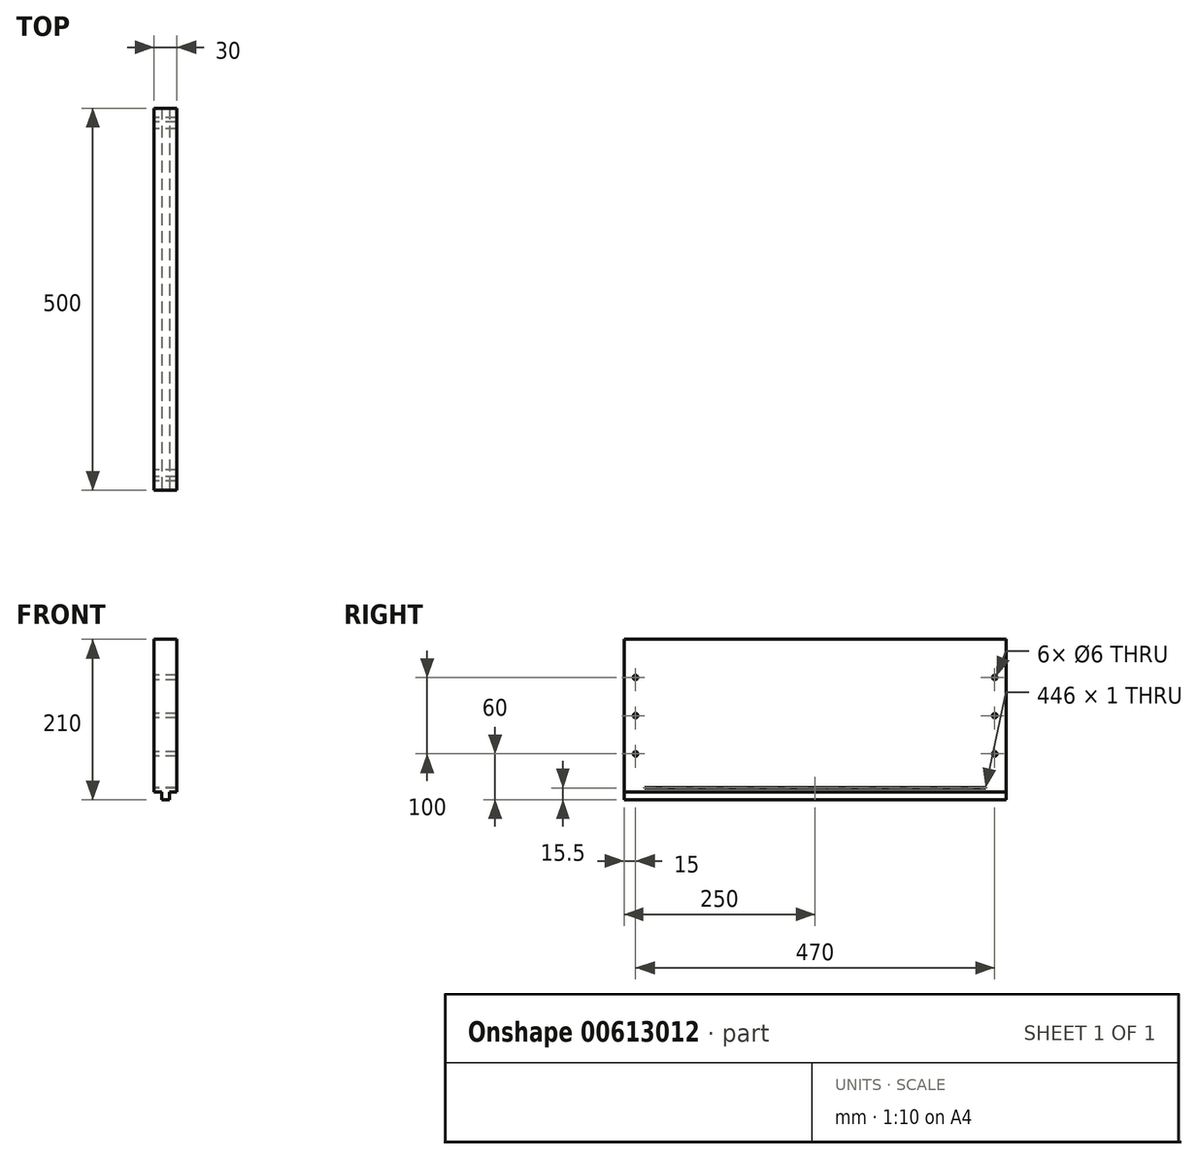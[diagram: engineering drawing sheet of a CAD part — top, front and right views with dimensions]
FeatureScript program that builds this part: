
annotation { "Feature Type Name" : "Feature", "Feature Type Description" : "" }
export const myFeature = defineFeature(function(context is Context, id is Id, definition is map)
    precondition{}
    {
        {
            var Q0;
            Q0=qCreatedBy(makeId("Right.planeOp"),FACE);
            var sketch = newSketch(context, id + "F0", { "sketchPlane" : qUnion([Q0])});
            skLineSegment(sketch, "E0.bottom", {"start": v(250, -100) * mm, "end": v(-250, -100) * mm});
            skLineSegment(sketch, "E0.top", {"start": v(250, 100) * mm, "end": v(-250, 100) * mm});
            skLineSegment(sketch, "E0.left", {"start": v(250, -100) * mm, "end": v(250, 100) * mm});
            skLineSegment(sketch, "E0.right", {"start": v(-250, -100) * mm, "end": v(-250, 100) * mm});
            skPoint(sketch, "E0.middle", {"position": v(0, 0) * mm});
            skCircle(sketch, "E1", {"center": v(-235, 50) * mm, "radius": 3 * mm});
            skCircle(sketch, "E2", {"center": v(235, -50) * mm, "radius": 3 * mm});
            skCircle(sketch, "E3", {"center": v(235, 50) * mm, "radius": 3 * mm});
            skCircle(sketch, "E4", {"center": v(-235, -50) * mm, "radius": 3 * mm});
            skCircle(sketch, "E5", {"center": v(-235, 0) * mm, "radius": 3 * mm});
            skCircle(sketch, "E6", {"center": v(235, 0) * mm, "radius": 3 * mm});
            skSolve(sketch);
        }
        {
            var Q0;
            Q0=qSketchRegion(id+"F0",true);
            extrude(context, id + "F1", {"entities" : qUnion([Q0]), "depth" : 30 * mm, "offsetDistance" : 25 * mm});
        }
        {
            var Q0;
            Q0=makeQuery(id+"F1.opExtrude","SWEPT_FACE",FACE,{"disambiguationData":[OSD([sQuery(id+"F0.wireOp",EDGE,"E0.right")])]});
            var sketch = newSketch(context, id + "F2", { "sketchPlane" : qUnion([Q0])});
            skLineSegment(sketch, "E7.bottom", {"start": v(20, -110) * mm, "end": v(10, -110) * mm});
            skLineSegment(sketch, "E7.top", {"start": v(20, -100) * mm, "end": v(10, -100) * mm});
            skLineSegment(sketch, "E7.left", {"start": v(20, -110) * mm, "end": v(20, -100) * mm});
            skLineSegment(sketch, "E7.right", {"start": v(10, -110) * mm, "end": v(10, -100) * mm});
            skPoint(sketch, "E7.middle", {"position": v(15, -105) * mm});
            skSolve(sketch);
        }
        {
            var Q0;
            Q0=qSketchRegion(id+"F2",true);
            extrude(context, id + "F3", {"entities" : qUnion([Q0]), "operationType" : NewBodyOperationType.ADD, "oppositeDirection" : true, "depth" : 500 * mm, "offsetDistance" : 25 * mm});
        }
        {
            var Q0;
            Q0=makeQuery(id+"F3.boolean.opBoolean","MERGE",FACE,{"derivedFrom":[makeQuery(id+"F1.opExtrude","SWEPT_FACE",FACE,{"disambiguationData":[OSD([sQuery(id+"F0.wireOp",EDGE,"E0.right")])]}),makeQuery(id+"F3.opExtrude","CAP_FACE",FACE,{"disambiguationData":[OSD([sQuery(id+"F2.wireOp",EDGE,"E7.bottom"),sQuery(id+"F2.wireOp",EDGE,"E7.top"),sQuery(id+"F2.wireOp",EDGE,"E7.left"),sQuery(id+"F2.wireOp",EDGE,"E7.right")])],"isStart":true})]});
            var sketch = newSketch(context, id + "F4", { "sketchPlane" : qUnion([Q0])});
            skLineSegment(sketch, "E8.bottom", {"start": v(30, -95) * mm, "end": v(0, -95) * mm});
            skLineSegment(sketch, "E8.top", {"start": v(30, -94) * mm, "end": v(0, -94) * mm});
            skLineSegment(sketch, "E8.left", {"start": v(30, -95) * mm, "end": v(30, -94) * mm});
            skLineSegment(sketch, "E8.right", {"start": v(0, -95) * mm, "end": v(0, -94) * mm});
            skPoint(sketch, "E8.middle", {"position": v(15, -94.5) * mm});
            skSolve(sketch);
        }
        {
            var Q0;
            Q0=qSketchRegion(id+"F4",true);
            extrude(context, id + "F5", {"entities" : qUnion([Q0]), "operationType" : NewBodyOperationType.REMOVE, "oppositeDirection" : true, "depth" : 473 * mm, "offsetDistance" : 25 * mm, "hasSecondDirection" : true, "secondDirectionOppositeDirection" : true, "secondDirectionDepth" : 27 * mm});
        }
    });
